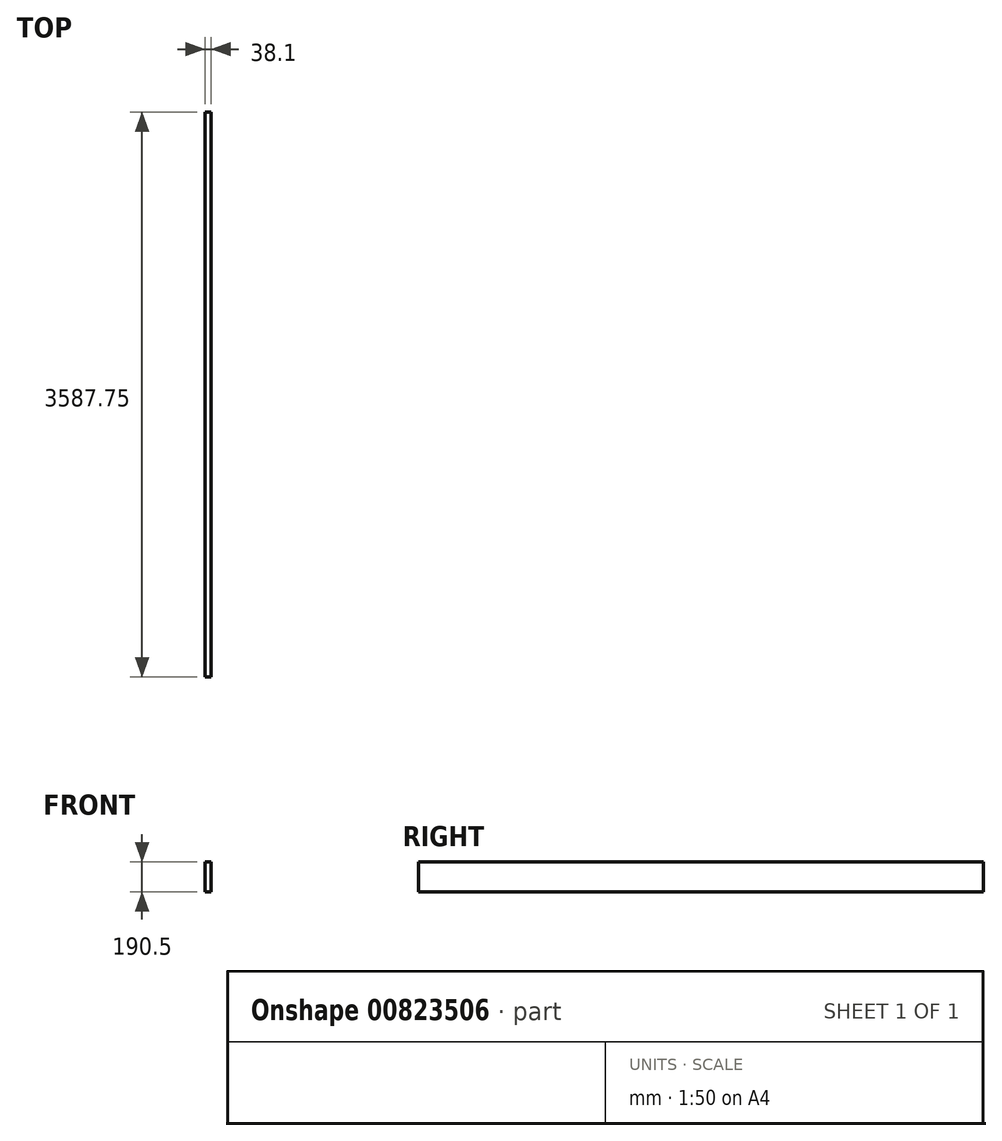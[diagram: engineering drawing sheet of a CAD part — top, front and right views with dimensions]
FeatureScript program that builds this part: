
annotation { "Feature Type Name" : "Feature", "Feature Type Description" : "" }
export const myFeature = defineFeature(function(context is Context, id is Id, definition is map)
    precondition{}
    {
        {
            var Q0;
            Q0=qCreatedBy(makeId("Front.planeOp"),FACE);
            var sketch = newSketch(context, id + "F0", { "sketchPlane" : qUnion([Q0])});
            skLineSegment(sketch, "E0.bottom", {"start": v(0, 0) * mm, "end": v(38.1, 0) * mm});
            skLineSegment(sketch, "E0.top", {"start": v(0, 190.5) * mm, "end": v(38.1, 190.5) * mm});
            skLineSegment(sketch, "E0.left", {"start": v(0, 0) * mm, "end": v(0, 190.5) * mm});
            skLineSegment(sketch, "E0.right", {"start": v(38.1, 0) * mm, "end": v(38.1, 190.5) * mm});
            skSolve(sketch);
        }
        {
            var Q0;
            Q0=qSketchRegion(id+"F0",true);
            extrude(context, id + "F1", {"entities" : qUnion([Q0]), "depth" : 3587.75 * mm, "offsetDistance" : 25.4 * mm});
        }
    });
